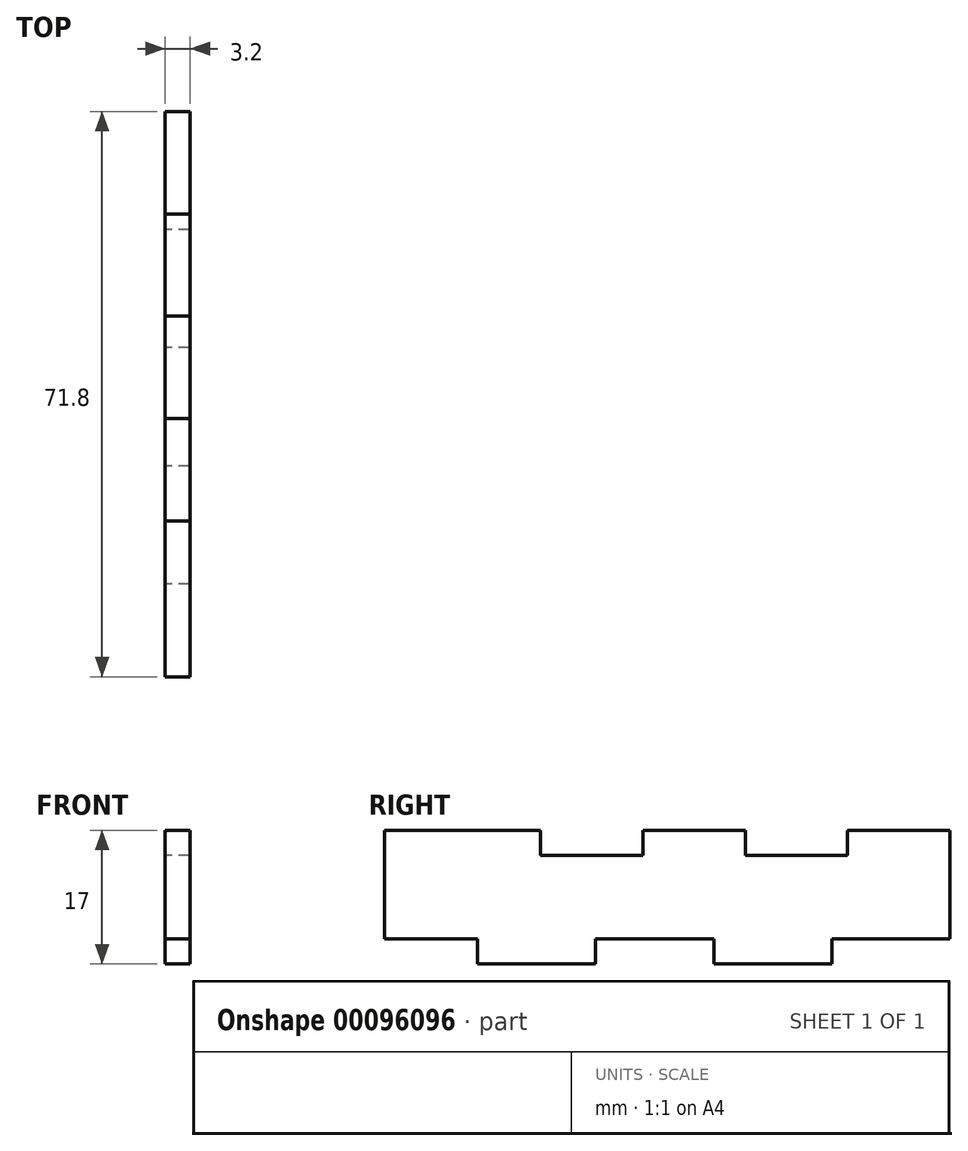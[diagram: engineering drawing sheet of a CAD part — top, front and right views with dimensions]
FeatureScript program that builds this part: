
annotation { "Feature Type Name" : "Feature", "Feature Type Description" : "" }
export const myFeature = defineFeature(function(context is Context, id is Id, definition is map)
    precondition{}
    {
        {
            var Q0;
            Q0=qCreatedBy(makeId("Right.planeOp"),FACE);
            var sketch = newSketch(context, id + "F0", { "sketchPlane" : qUnion([Q0])});
            skPoint(sketch, "E0.middle", {"position": v(0, 0) * mm});
            skLineSegment(sketch, "E1", {"start": v(22.5, -6) * mm, "end": v(22.5, -2.8) * mm});
            skLineSegment(sketch, "E2", {"start": v(7.5, -2.8) * mm, "end": v(7.5, -6) * mm});
            skLineSegment(sketch, "E3", {"start": v(-7.5, -6) * mm, "end": v(-7.5, -2.8) * mm});
            skLineSegment(sketch, "E4", {"start": v(-34.3, 11) * mm, "end": v(-34.3, 4.1) * mm});
            skLineSegment(sketch, "E5", {"start": v(-34.3, -0.9) * mm, "end": v(-34.3, -2.8) * mm});
            skLineSegment(sketch, "E6", {"start": v(-34.3, 11) * mm, "end": v(-14.5, 11) * mm});
            skLineSegment(sketch, "E7", {"start": v(-14.5, 11) * mm, "end": v(-14.5, 7.8) * mm});
            skLineSegment(sketch, "E8", {"start": v(-14.5, 7.8) * mm, "end": v(-1.5, 7.8) * mm});
            skLineSegment(sketch, "E9", {"start": v(-1.5, 7.8) * mm, "end": v(-1.5, 11) * mm});
            skLineSegment(sketch, "E10", {"start": v(11.5, 11) * mm, "end": v(11.5, 7.8) * mm});
            skLineSegment(sketch, "E11", {"start": v(11.5, 7.8) * mm, "end": v(24.5, 7.8) * mm});
            skLineSegment(sketch, "E12", {"start": v(24.5, 7.8) * mm, "end": v(24.5, 11) * mm});
            skLineSegment(sketch, "E13", {"start": v(24.5, 11) * mm, "end": v(37.5, 11) * mm});
            skLineSegment(sketch, "E14", {"start": v(37.5, 11) * mm, "end": v(37.5, -2.8) * mm});
            skLineSegment(sketch, "E15", {"start": v(22.5, -6) * mm, "end": v(7.5, -6) * mm});
            skLineSegment(sketch, "E16", {"start": v(22.5, -2.8) * mm, "end": v(37.5, -2.8) * mm});
            skLineSegment(sketch, "E17", {"start": v(7.5, -2.8) * mm, "end": v(-7.5, -2.8) * mm});
            skLineSegment(sketch, "E18.trimOffspring", {"start": v(-7.5, -6) * mm, "end": v(-22.5, -6) * mm});
            skLineSegment(sketch, "E19", {"start": v(-22.5, -6) * mm, "end": v(-22.5, -2.8) * mm});
            skLineSegment(sketch, "E20", {"start": v(-22.5, -2.8) * mm, "end": v(-34.3, -2.8) * mm});
            skLineSegment(sketch, "E21", {"start": v(-22.5, -6) * mm, "end": v(-43.47, -6) * mm, "construction": true});
            skLineSegment(sketch, "E22", {"start": v(-1.5, 11) * mm, "end": v(11.5, 11) * mm});
            skLineSegment(sketch, "E23", {"start": v(-34.3, 4.1) * mm, "end": v(-34.3, -0.9) * mm});
            skSolve(sketch);
        }
        {
            var Q0;
            Q0=makeQuery(id+"F0.imprint","IMPRINT",FACE,{"disambiguationData":[TD([[makeQuery(id+"F0.imprint","IMPRINT",EDGE,{"derivedFrom":sQuery(id+"F0.wireOp",EDGE,"E1")}),1.0]])]});
            extrude(context, id + "F1", {"entities" : qUnion([Q0]), "endBound" : BoundingType.SYMMETRIC, "depth" : 3.2 * mm});
        }
    });
